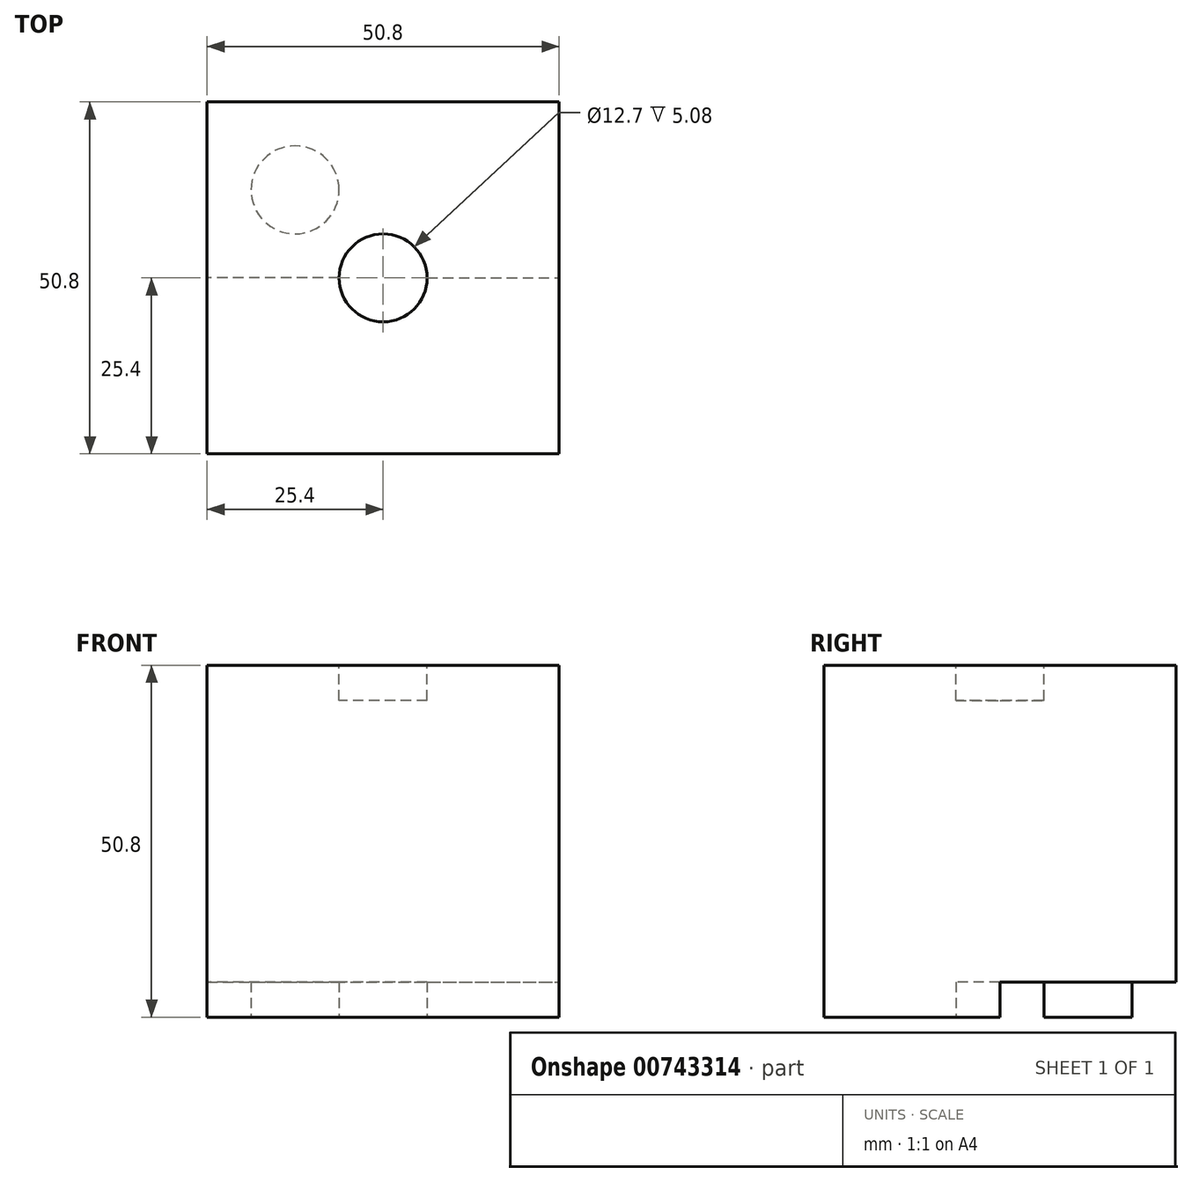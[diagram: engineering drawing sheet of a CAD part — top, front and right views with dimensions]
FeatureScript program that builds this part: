
annotation { "Feature Type Name" : "Feature", "Feature Type Description" : "" }
export const myFeature = defineFeature(function(context is Context, id is Id, definition is map)
    precondition{}
    {
        {
            var Q0;
            Q0=qCreatedBy(makeId("Front.planeOp"),FACE);
            var sketch = newSketch(context, id + "F0", { "sketchPlane" : qUnion([Q0])});
            skLineSegment(sketch, "E0", {"start": v(0, 0) * mm, "end": v(-25.4, 0) * mm});
            skLineSegment(sketch, "E1", {"start": v(-25.4, 0) * mm, "end": v(-25.4, 25.4) * mm});
            skLineSegment(sketch, "E2.bottom", {"start": v(-25.4, 25.4) * mm, "end": v(25.4, 25.4) * mm});
            skLineSegment(sketch, "E2.top", {"start": v(-25.4, -25.4) * mm, "end": v(25.4, -25.4) * mm});
            skLineSegment(sketch, "E2.left", {"start": v(-25.4, 25.4) * mm, "end": v(-25.4, -25.4) * mm});
            skLineSegment(sketch, "E2.right", {"start": v(25.4, 25.4) * mm, "end": v(25.4, -25.4) * mm});
            skSolve(sketch);
        }
        {
            var Q0;
            Q0 = qSketchRegion(id + "F0", true);
            extrude(context, id + "F1", {"entities" : qUnion([Q0]), "depth" : 25.4 * mm, "offsetDistance" : 25.4 * mm});
        }
        {
            var Q0;
            Q0=makeQuery(id+"F1.opExtrude","CAP_FACE",FACE,{"disambiguationData":[OSD([sQuery(id+"F0.wireOp",EDGE,"E2.bottom"),sQuery(id+"F0.wireOp",EDGE,"E2.top"),sQuery(id+"F0.wireOp",EDGE,"E2.left"),sQuery(id+"F0.wireOp",EDGE,"E2.right")])],"isStart":true});
            extrude(context, id + "F2", {"entities" : qUnion([Q0]), "operationType" : NewBodyOperationType.ADD, "depth" : 25.4 * mm, "offsetDistance" : 25.4 * mm});
        }
        {
            var Q0;
            {var subQ0=sQuery(id+"F0.wireOp",EDGE,"E2.bottom");Q0=makeQuery(id+"F2.boolean.opBoolean","MERGE",FACE,{"derivedFrom":[makeQuery(id+"F1.opExtrude","SWEPT_FACE",FACE,{"disambiguationData":[OSD([subQ0])]}),makeQuery(id+"F2.opExtrude","SWEPT_FACE",FACE,{"disambiguationData":[OSD([subQ0])]})]});}
            var sketch = newSketch(context, id + "F3", { "sketchPlane" : qUnion([Q0])});
            skPoint(sketch, "E3", {"position": v(0, 0) * mm});
            skCircle(sketch, "E4", {"center": v(0, 0) * mm, "radius": 6.35 * mm});
            skSolve(sketch);
        }
        {
            var Q0;
            Q0=makeQuery(id+"F3.imprint","IMPRINT",FACE,{"disambiguationData":[TD([[makeQuery(id+"F3.imprint","IMPRINT",EDGE,{"derivedFrom":sQuery(id+"F3.wireOp",EDGE,"E4")}),1.0]])]});
            extrude(context, id + "F4", {"entities" : qUnion([Q0]), "operationType" : NewBodyOperationType.REMOVE, "oppositeDirection" : true, "depth" : 5.08 * mm, "offsetDistance" : 25.4 * mm});
        }
        {
            var Q0;
            Q0=makeQuery(id+"F2.opExtrude","CAP_FACE",FACE,{"disambiguationData":[OSD([sQuery(id+"F0.wireOp",EDGE,"E2.bottom"),sQuery(id+"F0.wireOp",EDGE,"E2.top"),sQuery(id+"F0.wireOp",EDGE,"E2.left"),sQuery(id+"F0.wireOp",EDGE,"E2.right")])],"isStart":false});
            var sketch = newSketch(context, id + "F5", { "sketchPlane" : qUnion([Q0])});
            skLineSegment(sketch, "E5", {"start": v(0, 0) * mm, "end": v(-25.4, 0) * mm});
            skLineSegment(sketch, "E6", {"start": v(-25.4, 0) * mm, "end": v(-12.7, 0) * mm});
            skLineSegment(sketch, "E7", {"start": v(-12.7, 0) * mm, "end": v(-12.7, 25.4) * mm});
            skLineSegment(sketch, "E8", {"start": v(-12.7, 25.4) * mm, "end": v(-12.7, 0) * mm});
            skLineSegment(sketch, "E9", {"start": v(0, 0) * mm, "end": v(25.4, 0) * mm});
            skLineSegment(sketch, "E10", {"start": v(25.4, 0) * mm, "end": v(12.7, 0) * mm});
            skLineSegment(sketch, "E11", {"start": v(12.7, 0) * mm, "end": v(12.7, -25.4) * mm});
            skPoint(sketch, "E12", {"position": v(-12.7, 12.7) * mm});
            skPoint(sketch, "E13", {"position": v(12.7, -12.7) * mm});
            skCircle(sketch, "E14", {"center": v(-12.7, 12.7) * mm, "radius": 6.35 * mm});
            skCircle(sketch, "E15", {"center": v(12.7, -12.7) * mm, "radius": 6.46 * mm});
            skSolve(sketch);
        }
        {
            var Q0;
            {var subQ0=sQuery(id+"F5.wireOp",EDGE,"E14");var subQ1=sQuery(id+"F5.wireOp",EDGE,"E8");var subQ2=makeQuery(id+"F5.imprint","INTERSECT",VERTEX,{"disambiguationData":[OD(0.0)],"derivedFrom":[subQ1,subQ0]});Q0=makeQuery(id+"F5.imprint","IMPRINT",FACE,{"disambiguationData":[TD([[makeQuery(id+"F5.imprint","IMPRINT",EDGE,{"disambiguationData":[TD([[subQ2,-1.0]])],"derivedFrom":subQ1}),-1.0]])]});}
            var Q1;
            {var subQ0=sQuery(id+"F5.wireOp",EDGE,"E14");var subQ1=sQuery(id+"F5.wireOp",EDGE,"E8");var subQ2=makeQuery(id+"F5.imprint","INTERSECT",VERTEX,{"disambiguationData":[OD(0.0)],"derivedFrom":[subQ1,subQ0]});Q1=makeQuery(id+"F5.imprint","IMPRINT",FACE,{"disambiguationData":[TD([[makeQuery(id+"F5.imprint","IMPRINT",EDGE,{"disambiguationData":[TD([[subQ2,-1.0]])],"derivedFrom":subQ1}),1.0]])]});}
            var Q2;
            {var subQ0=sQuery(id+"F5.wireOp",EDGE,"E15");var subQ1=sQuery(id+"F5.wireOp",EDGE,"E11");var subQ2=makeQuery(id+"F5.imprint","INTERSECT",VERTEX,{"disambiguationData":[OD(0.0)],"derivedFrom":[subQ1,subQ0]});Q2=makeQuery(id+"F5.imprint","IMPRINT",FACE,{"disambiguationData":[TD([[makeQuery(id+"F5.imprint","IMPRINT",EDGE,{"disambiguationData":[TD([[subQ2,-1.0]])],"derivedFrom":subQ1}),1.0]])]});}
            var Q3;
            {var subQ0=sQuery(id+"F5.wireOp",EDGE,"E15");var subQ1=sQuery(id+"F5.wireOp",EDGE,"E11");var subQ2=makeQuery(id+"F5.imprint","INTERSECT",VERTEX,{"disambiguationData":[OD(0.0)],"derivedFrom":[subQ1,subQ0]});Q3=makeQuery(id+"F5.imprint","IMPRINT",FACE,{"disambiguationData":[TD([[makeQuery(id+"F5.imprint","IMPRINT",EDGE,{"disambiguationData":[TD([[subQ2,-1.0]])],"derivedFrom":subQ1}),-1.0]])]});}
            extrude(context, id + "F6", {"entities" : qUnion([Q0, Q1, Q2, Q3]), "operationType" : NewBodyOperationType.REMOVE, "oppositeDirection" : true, "depth" : 5.08 * mm, "offsetDistance" : 25.4 * mm});
        }
        {
            var Q0;
            {var subQ0=sQuery(id+"F0.wireOp",EDGE,"E2.top");Q0=makeQuery(id+"F2.boolean.opBoolean","MERGE",FACE,{"derivedFrom":[makeQuery(id+"F1.opExtrude","SWEPT_FACE",FACE,{"disambiguationData":[OSD([subQ0])]}),makeQuery(id+"F2.opExtrude","SWEPT_FACE",FACE,{"disambiguationData":[OSD([subQ0])]})]});}
            var sketch = newSketch(context, id + "F7", { "sketchPlane" : qUnion([Q0])});
            skLineSegment(sketch, "E16", {"start": v(0, 0) * mm, "end": v(25.4, 0) * mm});
            skLineSegment(sketch, "E17", {"start": v(25.4, 0) * mm, "end": v(12.7, 0) * mm});
            skLineSegment(sketch, "E18", {"start": v(12.7, 0) * mm, "end": v(12.7, 25.4) * mm});
            skLineSegment(sketch, "E19", {"start": v(12.7, 25.4) * mm, "end": v(12.7, 12.7) * mm});
            skLineSegment(sketch, "E20", {"start": v(12.7, 12.7) * mm, "end": v(12.7, 0) * mm});
            skLineSegment(sketch, "E21", {"start": v(0, 0) * mm, "end": v(-25.4, 0) * mm});
            skLineSegment(sketch, "E22", {"start": v(-25.4, 0) * mm, "end": v(-12.7, 0) * mm});
            skLineSegment(sketch, "E23", {"start": v(-12.7, 0) * mm, "end": v(-12.7, -25.4) * mm});
            skLineSegment(sketch, "E24", {"start": v(-12.7, -25.4) * mm, "end": v(-12.7, -12.7) * mm});
            skPoint(sketch, "E25", {"position": v(-12.7, -12.7) * mm});
            skPoint(sketch, "E26", {"position": v(12.7, 12.7) * mm});
            skCircle(sketch, "E27", {"center": v(-12.7, -12.7) * mm, "radius": 6.35 * mm});
            skCircle(sketch, "E28", {"center": v(12.7, 12.7) * mm, "radius": 6.35 * mm});
            skCircle(sketch, "E29", {"center": v(0, 0) * mm, "radius": 6.35 * mm});
            skSolve(sketch);
        }
        {
            var Q0;
            {var subQ0=sQuery(id+"F7.wireOp",EDGE,"E24");var subQ1=sQuery(id+"F7.wireOp",EDGE,"E23");var subQ2=makeQuery(id+"F7.imprint","INTERSECT",VERTEX,{"derivedFrom":[subQ1,subQ0]});Q0=makeQuery(id+"F7.imprint","IMPRINT",FACE,{"disambiguationData":[TD([[makeQuery(id+"F7.imprint","IMPRINT",EDGE,{"disambiguationData":[TD([[subQ2,1.0]])],"derivedFrom":subQ1}),-1.0]])]});}
            var Q1;
            {var subQ0=sQuery(id+"F7.wireOp",EDGE,"E24");var subQ1=sQuery(id+"F7.wireOp",EDGE,"E23");var subQ2=makeQuery(id+"F7.imprint","INTERSECT",VERTEX,{"derivedFrom":[subQ1,subQ0]});Q1=makeQuery(id+"F7.imprint","IMPRINT",FACE,{"disambiguationData":[TD([[makeQuery(id+"F7.imprint","IMPRINT",EDGE,{"disambiguationData":[TD([[subQ2,1.0]])],"derivedFrom":subQ1}),1.0]])]});}
            var Q2;
            {var subQ0=sQuery(id+"F7.wireOp",EDGE,"E21");var subQ1=sQuery(id+"F7.wireOp",EDGE,"E16");var subQ2=makeQuery(id+"F7.imprint","INTERSECT",VERTEX,{"derivedFrom":[subQ1,subQ0]});Q2=makeQuery(id+"F7.imprint","IMPRINT",FACE,{"disambiguationData":[TD([[makeQuery(id+"F7.imprint","IMPRINT",EDGE,{"disambiguationData":[TD([[subQ2,-1.0]])],"derivedFrom":subQ1}),-1.0]])]});}
            var Q3;
            {var subQ0=sQuery(id+"F7.wireOp",EDGE,"E21");var subQ1=sQuery(id+"F7.wireOp",EDGE,"E16");var subQ2=makeQuery(id+"F7.imprint","INTERSECT",VERTEX,{"derivedFrom":[subQ1,subQ0]});Q3=makeQuery(id+"F7.imprint","IMPRINT",FACE,{"disambiguationData":[TD([[makeQuery(id+"F7.imprint","IMPRINT",EDGE,{"disambiguationData":[TD([[subQ2,-1.0]])],"derivedFrom":subQ1}),1.0]])]});}
            var Q4;
            {var subQ0=sQuery(id+"F7.wireOp",EDGE,"E20");var subQ1=sQuery(id+"F7.wireOp",EDGE,"E19");var subQ2=makeQuery(id+"F7.imprint","INTERSECT",VERTEX,{"derivedFrom":[subQ1,subQ0]});Q4=makeQuery(id+"F7.imprint","IMPRINT",FACE,{"disambiguationData":[TD([[makeQuery(id+"F7.imprint","IMPRINT",EDGE,{"disambiguationData":[TD([[subQ2,1.0]])],"derivedFrom":subQ1}),-1.0]])]});}
            var Q5;
            {var subQ0=sQuery(id+"F7.wireOp",EDGE,"E20");var subQ1=sQuery(id+"F7.wireOp",EDGE,"E19");var subQ2=makeQuery(id+"F7.imprint","INTERSECT",VERTEX,{"derivedFrom":[subQ1,subQ0]});Q5=makeQuery(id+"F7.imprint","IMPRINT",FACE,{"disambiguationData":[TD([[makeQuery(id+"F7.imprint","IMPRINT",EDGE,{"disambiguationData":[TD([[subQ2,1.0]])],"derivedFrom":subQ1}),1.0]])]});}
            extrude(context, id + "F8", {"entities" : qUnion([Q0, Q1, Q2, Q3, Q4, Q5]), "operationType" : NewBodyOperationType.REMOVE, "oppositeDirection" : true, "depth" : 5.08 * mm, "offsetDistance" : 25.4 * mm});
        }
        {
            var Q0;
            {var subQ0=sQuery(id+"F5.wireOp",EDGE,"E14");var subQ1=sQuery(id+"F5.wireOp",EDGE,"E8");var subQ2=makeQuery(id+"F5.imprint","INTERSECT",VERTEX,{"disambiguationData":[OD(0.0)],"derivedFrom":[subQ1,subQ0]});Q0=makeQuery(id+"F5.imprint","IMPRINT",FACE,{"disambiguationData":[TD([[makeQuery(id+"F5.imprint","IMPRINT",EDGE,{"disambiguationData":[TD([[subQ2,-1.0]])],"derivedFrom":subQ1}),-1.0]])]});}
            var Q1;
            {var subQ0=sQuery(id+"F5.wireOp",EDGE,"E15");var subQ1=sQuery(id+"F5.wireOp",EDGE,"E11");var subQ2=makeQuery(id+"F5.imprint","INTERSECT",VERTEX,{"disambiguationData":[OD(0.0)],"derivedFrom":[subQ1,subQ0]});Q1=makeQuery(id+"F5.imprint","IMPRINT",FACE,{"disambiguationData":[TD([[makeQuery(id+"F5.imprint","IMPRINT",EDGE,{"disambiguationData":[TD([[subQ2,-1.0]])],"derivedFrom":subQ1}),-1.0]])]});}
            var Q2;
            {var subQ0=sQuery(id+"F5.wireOp",EDGE,"E15");var subQ1=sQuery(id+"F5.wireOp",EDGE,"E11");var subQ2=makeQuery(id+"F5.imprint","INTERSECT",VERTEX,{"disambiguationData":[OD(0.0)],"derivedFrom":[subQ1,subQ0]});Q2=makeQuery(id+"F5.imprint","IMPRINT",FACE,{"disambiguationData":[TD([[makeQuery(id+"F5.imprint","IMPRINT",EDGE,{"disambiguationData":[TD([[subQ2,-1.0]])],"derivedFrom":subQ1}),1.0]])]});}
            var Q3;
            {var subQ0=sQuery(id+"F5.wireOp",EDGE,"E14");var subQ1=sQuery(id+"F5.wireOp",EDGE,"E8");var subQ2=makeQuery(id+"F5.imprint","INTERSECT",VERTEX,{"disambiguationData":[OD(0.0)],"derivedFrom":[subQ1,subQ0]});Q3=makeQuery(id+"F5.imprint","IMPRINT",FACE,{"disambiguationData":[TD([[makeQuery(id+"F5.imprint","IMPRINT",EDGE,{"disambiguationData":[TD([[subQ2,-1.0]])],"derivedFrom":subQ1}),1.0]])]});}
            extrude(context, id + "F9", {"entities" : qUnion([Q0, Q1, Q2, Q3]), "operationType" : NewBodyOperationType.ADD, "oppositeDirection" : true, "depth" : 6.35 * mm, "offsetDistance" : 25.4 * mm});
        }
    });
